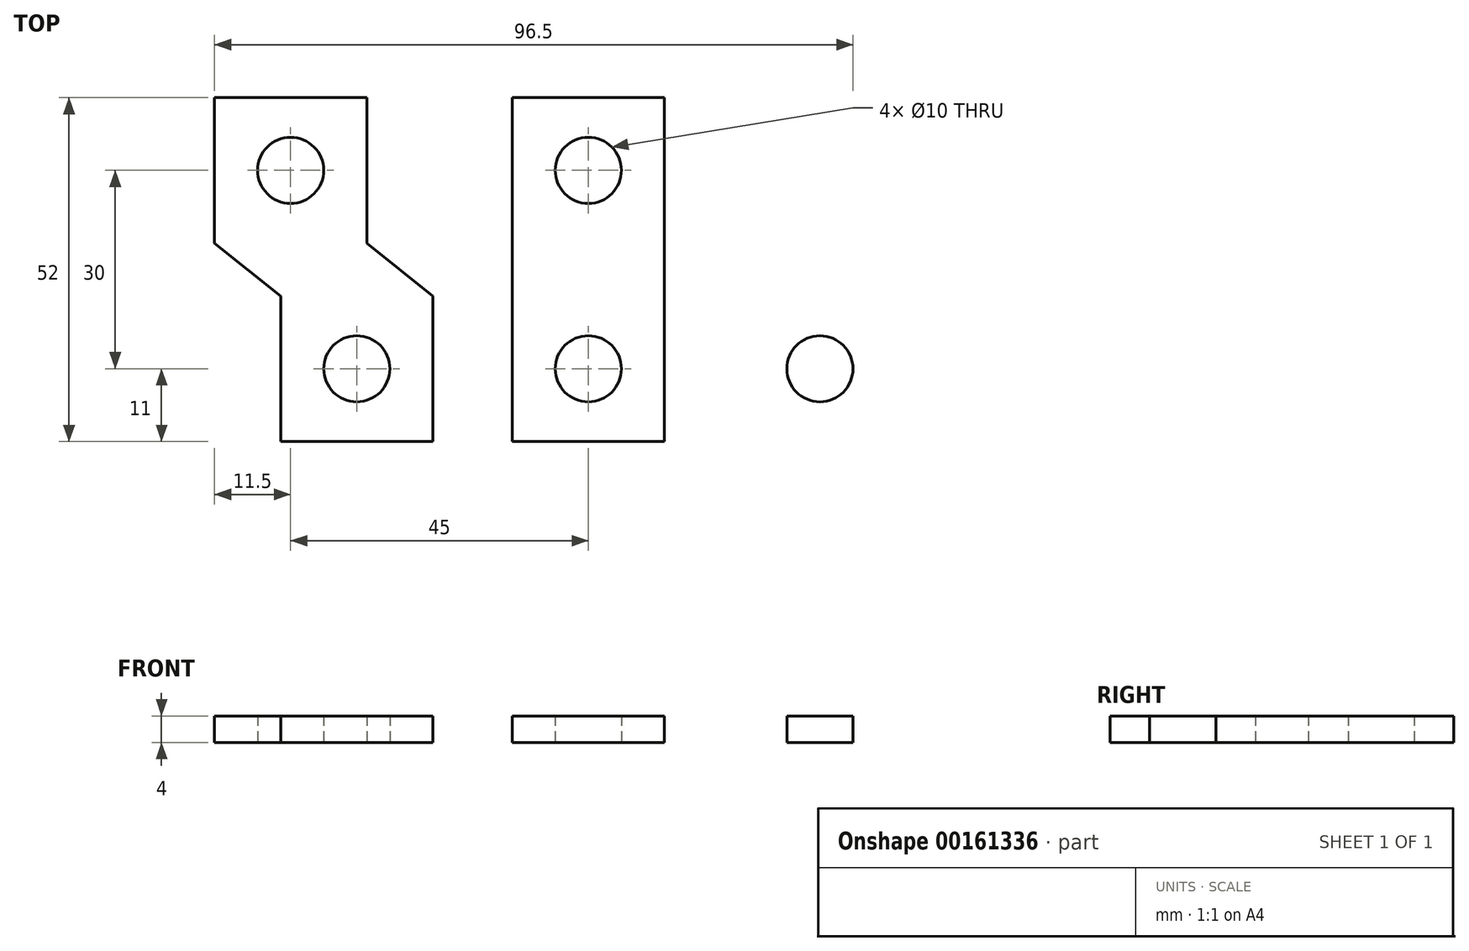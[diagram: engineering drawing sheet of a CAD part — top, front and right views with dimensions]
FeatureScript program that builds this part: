
annotation { "Feature Type Name" : "Feature", "Feature Type Description" : "" }
export const myFeature = defineFeature(function(context is Context, id is Id, definition is map)
    precondition{}
    {
        {
            var Q0;
            Q0=qCreatedBy(makeId("Top.planeOp"),FACE);
            var sketch = newSketch(context, id + "F0", { "sketchPlane" : qUnion([Q0])});
            skLineSegment(sketch, "E0.bottom", {"start": v(11.5, 26) * mm, "end": v(-11.5, 26) * mm});
            skLineSegment(sketch, "E0.top", {"start": v(11.5, -26) * mm, "end": v(-11.5, -26) * mm});
            skLineSegment(sketch, "E0.left", {"start": v(11.5, 26) * mm, "end": v(11.5, -26) * mm});
            skLineSegment(sketch, "E0.right", {"start": v(-11.5, 26) * mm, "end": v(-11.5, -26) * mm});
            skPoint(sketch, "E0.middle", {"position": v(0, 0) * mm});
            skLineSegment(sketch, "E1.bottom", {"start": v(-23.5, -26) * mm, "end": v(-46.5, -26) * mm});
            skLineSegment(sketch, "E1.right", {"start": v(-46.5, -26) * mm, "end": v(-46.5, -4) * mm});
            skLineSegment(sketch, "E2.bottom", {"start": v(-56.5, 26) * mm, "end": v(-33.5, 26) * mm});
            skLineSegment(sketch, "E3", {"start": v(-56.5, 26) * mm, "end": v(-56.5, 4) * mm});
            skLineSegment(sketch, "E4", {"start": v(-56.5, 4) * mm, "end": v(-46.5, -4) * mm});
            skLineSegment(sketch, "E5", {"start": v(-33.5, 26) * mm, "end": v(-33.5, 4) * mm});
            skLineSegment(sketch, "E6", {"start": v(-23.5, -26) * mm, "end": v(-23.5, -4) * mm});
            skLineSegment(sketch, "E7", {"start": v(-33.5, 4) * mm, "end": v(-23.5, -4) * mm});
            skPoint(sketch, "E8", {"position": v(-35, -15) * mm});
            skPoint(sketch, "E8.positionSnap0", {"position": v(-35, -26) * mm});
            skPoint(sketch, "E9", {"position": v(-45, 15) * mm});
            skPoint(sketch, "E9.positionSnap0", {"position": v(-45, 26) * mm});
            skCircle(sketch, "E10", {"center": v(-45, 15) * mm, "radius": 5 * mm});
            skCircle(sketch, "E11", {"center": v(-35, -15) * mm, "radius": 5 * mm});
            skPoint(sketch, "E12", {"position": v(0, 15) * mm});
            skPoint(sketch, "E12.positionSnap0", {"position": v(0, 26) * mm});
            skPoint(sketch, "E12.positionSnap1", {"position": v(-33.5, 15) * mm});
            skPoint(sketch, "E13", {"position": v(0, -15) * mm});
            skPoint(sketch, "E13.positionSnap0", {"position": v(0, -26) * mm});
            skCircle(sketch, "E14", {"center": v(0, -15) * mm, "radius": 5 * mm});
            skCircle(sketch, "E15", {"center": v(0, 15) * mm, "radius": 5 * mm});
            skCircle(sketch, "E16.MirrorC", {"center": v(35, -15) * mm, "radius": 5 * mm});
            skLineSegment(sketch, "E17.MirrorCS", {"start": v(56.5, 26) * mm, "end": v(56.5, 4) * mm});
            skPoint(sketch, "E18.MirrorP", {"position": v(35, -26) * mm});
            skLineSegment(sketch, "E19.MirrorCS", {"start": v(33.5, 4) * mm, "end": v(23.5, -4) * mm});
            skPoint(sketch, "E20.MirrorP", {"position": v(33.5, 15) * mm});
            skLineSegment(sketch, "E21.MirrorCS", {"start": v(46.5, -26) * mm, "end": v(46.5, -4) * mm});
            skCircle(sketch, "E22.MirrorC", {"center": v(45, 15) * mm, "radius": 5 * mm});
            skLineSegment(sketch, "E23.MirrorCS", {"start": v(56.5, 26) * mm, "end": v(33.5, 26) * mm});
            skLineSegment(sketch, "E24.MirrorCS", {"start": v(33.5, 26) * mm, "end": v(33.5, 4) * mm});
            skLineSegment(sketch, "E25.MirrorCS", {"start": v(23.5, -26) * mm, "end": v(46.5, -26) * mm});
            skLineSegment(sketch, "E26.MirrorCS", {"start": v(23.5, -26) * mm, "end": v(23.5, -4) * mm});
            skPoint(sketch, "E27.MirrorP", {"position": v(45, 26) * mm});
            skLineSegment(sketch, "E28.MirrorCS", {"start": v(56.5, 4) * mm, "end": v(46.5, -4) * mm});
            skSolve(sketch);
        }
        {
            var Q0;
            Q0=makeQuery(id+"F0.imprint","IMPRINT",FACE,{"disambiguationData":[TD([[makeQuery(id+"F0.imprint","IMPRINT",EDGE,{"derivedFrom":sQuery(id+"F0.wireOp",EDGE,"E1.bottom")}),-1.0]])]});
            var Q1;
            Q1=makeQuery(id+"F0.imprint","IMPRINT",FACE,{"disambiguationData":[TD([[makeQuery(id+"F0.imprint","IMPRINT",EDGE,{"derivedFrom":sQuery(id+"F0.wireOp",EDGE,"E0.bottom")}),1.0]])]});
            var Q2;
            Q2=makeQuery(id+"F0.imprint","IMPRINT",FACE,{"disambiguationData":[TD([[makeQuery(id+"F0.imprint","IMPRINT",EDGE,{"derivedFrom":sQuery(id+"F0.wireOp",EDGE,"c3188270-dda3-4326-a5e4-cba2b8a43d790.MirrorC")}),1.0]])]});
            var Q3;
            Q3=makeQuery(id+"F0.imprint","IMPRINT",FACE,{"disambiguationData":[TD([[makeQuery(id+"F0.imprint","IMPRINT",EDGE,{"derivedFrom":sQuery(id+"F0.wireOp",EDGE,"E16.MirrorC")}),1.0]])]});
            extrude(context, id + "F1", {"entities" : qUnion([Q0, Q1, Q2, Q3]), "depth" : 4 * mm});
        }
    });
